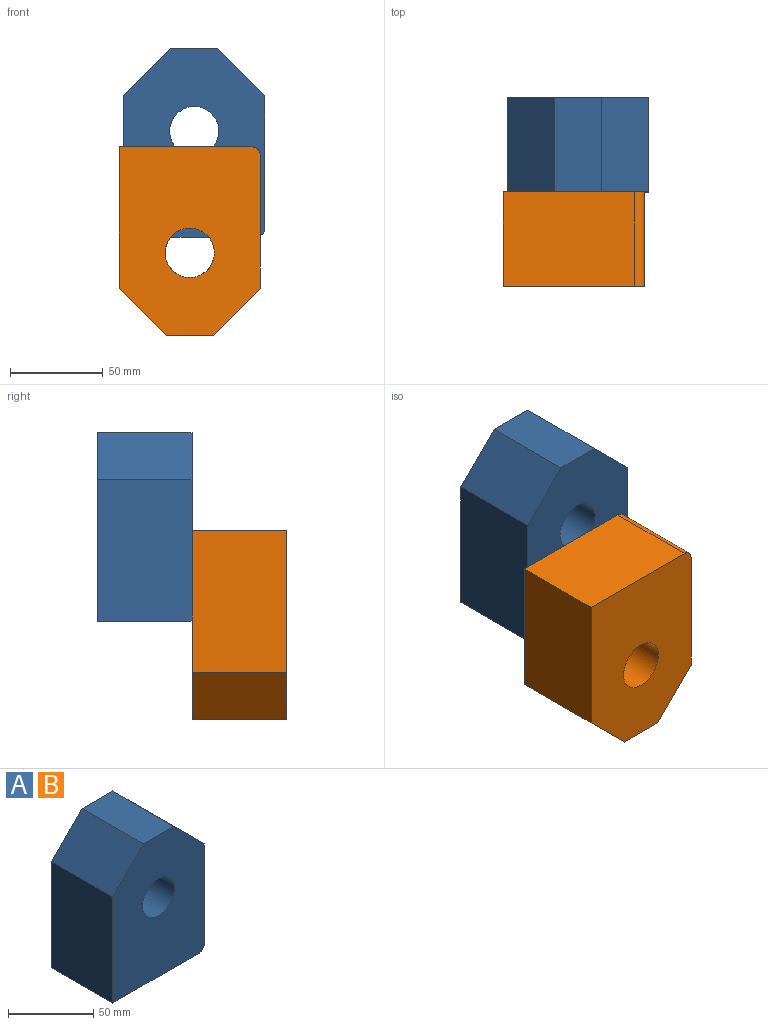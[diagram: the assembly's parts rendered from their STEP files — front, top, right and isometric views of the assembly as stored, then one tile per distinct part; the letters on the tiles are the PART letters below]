
ASSEMBLY  parts=2 mates=1
PART A: 10 faces, bbox 76.2x50.8x101.6 mm
  f0: plane 101.6x76.2mm, normal (0,1,0), area 6534.7mm2, adj f1,f3,f4,f5,f6,f7,f8,f9
  f1: plane 76.2x50.8mm, normal (-1,0,0), area 3871mm2, adj f0,f2,f5,f8
  f2: plane 101.6x76.2mm, normal (0,-1,0), area 6534.7mm2, adj f1,f3,f4,f5,f6,f7,f8,f9
  f3: plane 71.12x50.8mm, normal (1,0,0), area 3612.9mm2, adj f0,f2,f7,f9
  f4: plane 50.8x25.4mm, normal (0,0,1), area 1290.3mm2, adj f0,f2,f7,f8
  f5: plane 71.12x50.8mm, normal (0,0,-1), area 3612.9mm2, adj f0,f1,f2,f9
  f6: cylinder r=13.31mm len=50.8mm, axis (0,-1,0), area 4248.3mm2, adj f0,f2
  f7: plane 50.8x25.4mm, normal (0.71,0,0.71), area 1824.8mm2, adj f0,f2,f3,f4
  f8: plane 50.8x25.4mm, normal (-0.71,0,0.71), area 1824.8mm2, adj f0,f1,f2,f4
  f9: cylinder r=5.08mm len=50.8mm, axis (0,1,0), area 405.4mm2, adj f0,f2,f3,f5
PART B: same geometry as A
PLACE A t=(-26.15,8.36,-21.59)mm
PLACE B rot(axis=(1,0,0),180deg) t=(-28.61,-93.24,27.16)mm
MATE planar B.f2 <-> A.f2  axis (0,1,0) through (9.46,-42.44,-18.96)mm
